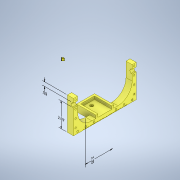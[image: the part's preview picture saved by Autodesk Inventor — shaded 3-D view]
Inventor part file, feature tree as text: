
AUTODESK INVENTOR PART (.ipt)
format: ipt  version: 2022 (Build 260153070, 153G)  size: 1,773,568 bytes
history: native  units: in
note: dims shown in document units (in); Inventor stores cm internally (conversion verified against a paired STEP export)
features: sketch x7, extrude x6, other x4, hole x2, mirror x2, fillet x1, split x1
ambient origin geometry x8: Origin, YZ Plane, XZ Plane, XY Plane, X Axis, Y Axis, Z Axis, Center Point
bodies: Solid1 (feature_tree)
feature tree (23):
  other  "Annotations"
  sketch  "Sketch1"  dims[d0=1.7in d1=4.25in]
  extrude  "Extrusion1"  Depth=4.25in
  extrude  "Extrusion2"  Depth=0.25in
  hole  "Hole1"  [1 undecoded]
  extrude  "Extrusion10"  TaperAngle=0.0deg  [1 undecoded]
  extrude  "Extrusion11"  Depth=0.5in
  extrude  "Extrusion12"  Depth=0.375in
  mirror  "Mirror8"
  fillet  "Fillet1"  Radius=0.375in
  extrude  "Extrusion13"  Depth=0.5in
  split  "Split1"
  hole  "Hole5"  [1 undecoded]
  mirror  "Mirror9"
  sketch  "Sketch2"  dims[d2=0.25in d3=0.25in]
  sketch  "Sketch15"  dims[d4=0.475in d5=0.0in]
  sketch  "Sketch16"  dims[d6=0.35in d7=0.0in]
  sketch  "Sketch17"  dims[d8=0.5in d9=0.5in]
  sketch  "Sketch18"  dims[d10=0.201in d11=0.75in d12=0.4in d13=0.1in d14=0.5635in d15=1.0in d16=0.8108in d17=0.375in d24=0.375in]
  sketch  "Sketch20"  dims[d101=2.75in d102=0.0in d103=0.5in d104=3.5in d105=0.0in d109=1.5in d115=0.0in d116=0.0in d117=1.75in d120=0.51in d140=0.05in d141=0.0in d142=3.225in d160=0.2375in d161=0.25in d162=0.25in d163=1.5748in d165=1.0in d166=0.3937in d168=1.0in d170=1.1811in d172=1.0in d173=0.3937in d175=1.0in d177=0.201in d178=0.75in d179=0.28in d180=0.2917in d181=0.5635in d182=1.0in d183=0.8108in d106=0.9428in d107=4.2237in d108=3.35in d125=0.0966in d126=0.3041in d127=2.97in d128=0.1855in d129=0.2047in d130=0.495in d119=0.5in d121=0.5in d122=0.0344in]
  other  "Linear Dimension 4"
  other  "Linear Dimension 6"
  other  "Linear Dimension 7"
note: 3 required parameter values undecoded (feature->parameter linkage not recoverable at this tier; creation-order binding heuristic only, values carry confidence <= 0.55)
